# Revit family: Haworth_Epure_Benches_withFixedLegs_DoubleEndModule_EU_PRELIMINARY
name_source: partatom
category: Furniture
units: mm (PartAtom-declared; Revit-internal decimal feet)

## family parameters
Always vertical = Yes
Cut with Voids When Loaded = No
OmniClass Number = 23.40.70.14.64.11
OmniClass Title = Office Furniture
Room Calculation Point = No
Shared = No
Work Plane-Based = No

## types (6) — shared parameters
Actual Height = 73 cm
Assembly Code = E2020200
Description = Haworth - Epure - Benches - Bench with Fixed Legs - Double End Module
Flip Top Finish = Haworth _ Paint _ Metallic Silver
Leg Height = 70 cm
Manufacturer = Haworth
Mobile Pedestal Hinged Door Opposite = No
Mobile Pedestal Opposite = No
Mobile Pedestal Sliding Door Opposite = No
Model = EUB5LXXXX
No Accessory Kit = No
Revision Number = 1
Security Drawer Opposite = No
Size = Verify Final Dim.w/ Haworth
Storage Options = Actual Width > 100 cm
Suspended Pedestal Open = No
Suspended Pedestal Open Opposite = No
Suspended Pedestal Open with Box Files = No
Suspended Pedestal Open with Pencil = No
Suspended Pedestal Open with Pencil Opposite = No
Trim Finish = Haworth _ Metal _ Structured White EC
URL = https://www.haworth.com
URL - Product = https://www.haworth.com
Upper Storage = Actual Width < 190 cm
Warranty = http://www.haworth.com
Worksurface Depth = 160, 180, 200 cm
Worksurface Width = 120, 140, 160, 180, 200 cm

## per-type parameters (varying)
- 120 x 160: Accessory Kit=Yes; Actual Depth=200 cm; Actual Width=233 cm; Cable Tray Double=Yes; Cable Tray Single=No; Cable Tray Width=183 cm; Central Rail=Yes; Depth=99 cm; Flip Top Cable Outlet=No; Mobile Pedestal=No; Mobile Pedestal Hinged Door=No; Mobile Pedestal Sliding Door=No; Rectangle=Yes; Right Side Storage=No; Right Side Storage Box File=No; Right Side Storage Box Open=No; Round Cable Outlet=No; Scallop=No; Security Drawer=No; Suspended Pedestal=Yes; Suspended Pedestal Open with Box Files Opposite=Yes; Suspended Pedestal Opposite=Yes; Upper Storage Desk Height Shelf=Yes; Upper Storage Nook Enclosed=No; Upper Storage Nook Enclosed Short=No; Upper Storage Nook Enclosed Tall=No; Upper Storage Nook Open=No; Void Depth=0 cm
- 200 x 160: Accessory Kit=Yes; Actual Depth=160 cm; Actual Width=200 cm; Cable Tray Double=No; Cable Tray Single=Yes; Cable Tray Width=150 cm; Central Rail=No; Depth=80 cm; Flip Top Cable Outlet=Yes; Mobile Pedestal=No; Mobile Pedestal Hinged Door=No; Mobile Pedestal Sliding Door=No; Rectangle=No; Right Side Storage=Yes; Right Side Storage Box File=No; Right Side Storage Box Open=Yes; Round Cable Outlet=No; Scallop=Yes; Security Drawer=Yes; Suspended Pedestal=No; Suspended Pedestal Open with Box Files Opposite=Yes; Suspended Pedestal Opposite=Yes; Upper Storage Desk Height Shelf=No; Upper Storage Nook Enclosed=No; Upper Storage Nook Enclosed Short=No; Upper Storage Nook Enclosed Tall=No; Upper Storage Nook Open=Yes; Void Depth=3 cm
- 140 x 180: Accessory Kit=Yes; Actual Depth=180 cm; Actual Width=140 cm; Cable Tray Double=Yes; Cable Tray Single=No; Cable Tray Width=90 cm; Central Rail=No; Depth=90 cm; Flip Top Cable Outlet=Yes; Mobile Pedestal=Yes; Mobile Pedestal Hinged Door=Yes; Mobile Pedestal Sliding Door=No; Rectangle=No; Right Side Storage=Yes; Right Side Storage Box File=No; Right Side Storage Box Open=Yes; Round Cable Outlet=No; Scallop=Yes; Security Drawer=No; Suspended Pedestal=No; Suspended Pedestal Open with Box Files Opposite=No; Suspended Pedestal Opposite=Yes; Upper Storage Desk Height Shelf=No; Upper Storage Nook Enclosed=Yes; Upper Storage Nook Enclosed Short=Yes; Upper Storage Nook Enclosed Tall=No; Upper Storage Nook Open=No; Void Depth=3 cm
- 180 x 180: Accessory Kit=No; Actual Depth=180 cm; Actual Width=180 cm; Cable Tray Double=Yes; Cable Tray Single=No; Cable Tray Width=130 cm; Central Rail=No; Depth=90 cm; Flip Top Cable Outlet=No; Mobile Pedestal=Yes; Mobile Pedestal Hinged Door=No; Mobile Pedestal Sliding Door=No; Rectangle=Yes; Right Side Storage=No; Right Side Storage Box File=No; Right Side Storage Box Open=No; Round Cable Outlet=No; Scallop=No; Security Drawer=No; Suspended Pedestal=No; Suspended Pedestal Open with Box Files Opposite=Yes; Suspended Pedestal Opposite=Yes; Upper Storage Desk Height Shelf=No; Upper Storage Nook Enclosed=Yes; Upper Storage Nook Enclosed Short=No; Upper Storage Nook Enclosed Tall=Yes; Upper Storage Nook Open=No; Void Depth=0 cm
- 160 x 200: Accessory Kit=Yes; Actual Depth=200 cm; Actual Width=160 cm; Cable Tray Double=No; Cable Tray Single=Yes; Cable Tray Width=110 cm; Central Rail=Yes; Depth=99 cm; Flip Top Cable Outlet=No; Mobile Pedestal=Yes; Mobile Pedestal Hinged Door=No; Mobile Pedestal Sliding Door=Yes; Rectangle=Yes; Right Side Storage=Yes; Right Side Storage Box File=Yes; Right Side Storage Box Open=No; Round Cable Outlet=Yes; Scallop=No; Security Drawer=No; Suspended Pedestal=No; Suspended Pedestal Open with Box Files Opposite=No; Suspended Pedestal Opposite=No; Upper Storage Desk Height Shelf=No; Upper Storage Nook Enclosed=No; Upper Storage Nook Enclosed Short=No; Upper Storage Nook Enclosed Tall=No; Upper Storage Nook Open=No; Void Depth=0 cm
- 200 x 200: Accessory Kit=Yes; Actual Depth=200 cm; Actual Width=233 cm; Cable Tray Double=Yes; Cable Tray Single=No; Cable Tray Width=183 cm; Central Rail=Yes; Depth=99 cm; Flip Top Cable Outlet=No; Mobile Pedestal=No; Mobile Pedestal Hinged Door=No; Mobile Pedestal Sliding Door=No; Rectangle=Yes; Right Side Storage=Yes; Right Side Storage Box File=Yes; Right Side Storage Box Open=No; Round Cable Outlet=No; Scallop=No; Security Drawer=No; Suspended Pedestal=Yes; Suspended Pedestal Open with Box Files Opposite=Yes; Suspended Pedestal Opposite=Yes; Upper Storage Desk Height Shelf=No; Upper Storage Nook Enclosed=No; Upper Storage Nook Enclosed Short=No; Upper Storage Nook Enclosed Tall=No; Upper Storage Nook Open=No; Void Depth=0 cm

## geometry (parser evidence)
native form markers: Blend x8, Sweep x43
no freeform markers — native parametric forms only
